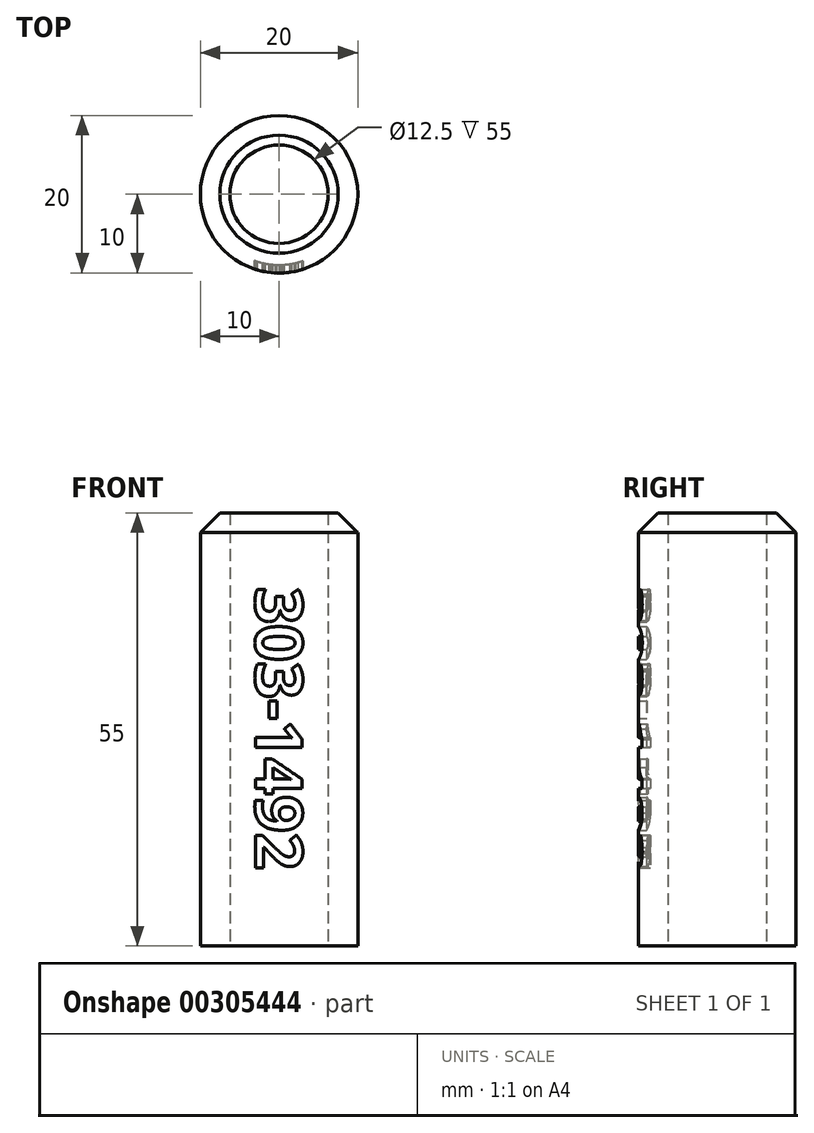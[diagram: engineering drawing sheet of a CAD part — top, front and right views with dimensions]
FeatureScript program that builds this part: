
annotation { "Feature Type Name" : "Feature", "Feature Type Description" : "" }
export const myFeature = defineFeature(function(context is Context, id is Id, definition is map)
    precondition{}
    {
        {
            assignVariable(context, id + "F0", {"name" : "protector_height", "anyValue" : 55 * mm});
        }
        {
            var Q0;
            Q0=qCreatedBy(makeId("Top.planeOp"),FACE);
            var sketch = newSketch(context, id + "F1", { "sketchPlane" : qUnion([Q0])});
            skCircle(sketch, "E0", {"center": v(0, 0) * mm, "radius": 6.25 * mm});
            skCircle(sketch, "E1", {"center": v(0, 0) * mm, "radius": 10 * mm});
            skSolve(sketch);
        }
        {
            var Q0;
            Q0 = qSketchRegion(id + "F1", true);
            extrude(context, id + "F2", {"entities" : qUnion([Q0]), "endBound" : BoundingType.SYMMETRIC, "depth" : getVariable(context, 'protector_height')});
        }
        {
            var Q0;
            Q0=makeQuery(id+"F2.opExtrude","CAP_EDGE",EDGE,{"disambiguationData":[OSD([sQuery(id+"F1.wireOp",EDGE,"E1")])],"isStart":false});
            chamfer(context, id + "F3", {"entities" : qUnion([Q0]), "width" : 2.5 * mm, "tangentPropagation" : true});
        }
        {
            var Q0;
            Q0=qCreatedBy(makeId("Front.planeOp"),FACE);
            var sketch = newSketch(context, id + "F4", { "sketchPlane" : qUnion([Q0])});
            skText(sketch, "E2", { "text": "303-1492", "fontName": "OpenSans-Bold.ttf"});
            const initialGuessF4  = {"E2": [-0.003, 0.01813, 0, -1, 0.006]};
            skSetInitialGuess(sketch, initialGuessF4);
            skSolve(sketch);
        }
        {
            var Q0;
            Q0 = qSketchRegion(id + "F4", true);
            extrude(context, id + "F5", {"entities" : qUnion([Q0]), "operationType" : NewBodyOperationType.REMOVE, "depth" : 25 * mm});
        }
        {
            var Q0;
            Q0=qCreatedBy(makeId("Top.planeOp"),FACE);
            var sketch = newSketch(context, id + "F6", { "sketchPlane" : qUnion([Q0])});
            skCircle(sketch, "E3", {"center": v(0, 0) * mm, "radius": 6.25 * mm});
            skCircle(sketch, "E4", {"center": v(0, 0) * mm, "radius": 9 * mm});
            skSolve(sketch);
        }
        {
            var Q0;
            Q0 = qSketchRegion(id + "F6", true);
            extrude(context, id + "F7", {"entities" : qUnion([Q0]), "operationType" : NewBodyOperationType.ADD, "endBound" : BoundingType.SYMMETRIC, "depth" : 45 * mm});
        }
    });
